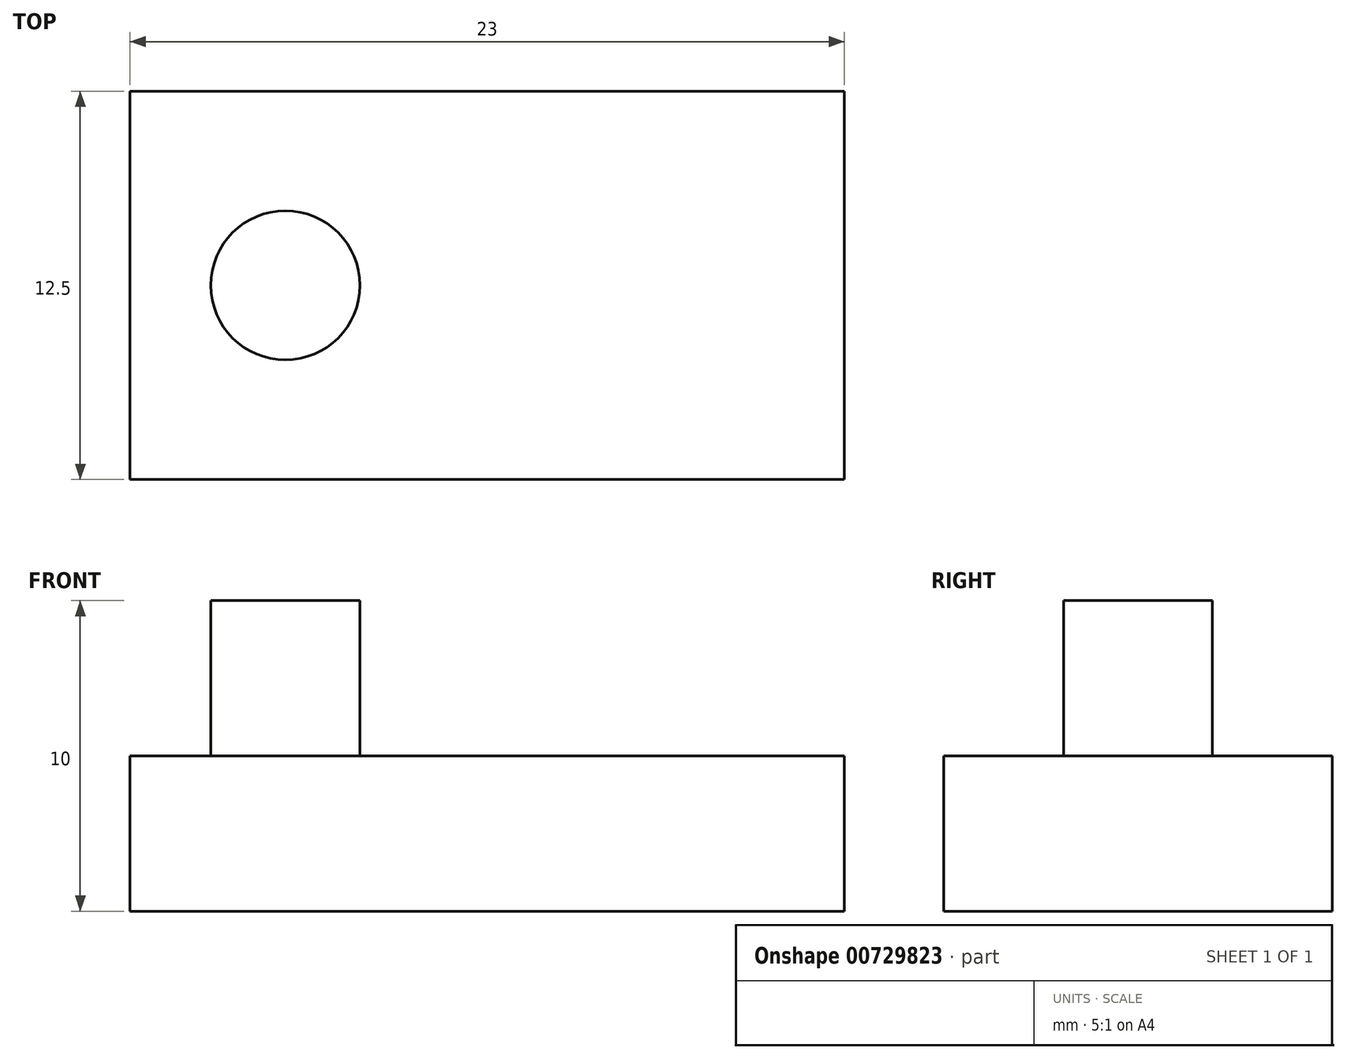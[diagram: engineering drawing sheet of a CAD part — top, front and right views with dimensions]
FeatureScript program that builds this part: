
annotation { "Feature Type Name" : "Feature", "Feature Type Description" : "" }
export const myFeature = defineFeature(function(context is Context, id is Id, definition is map)
    precondition{}
    {
        {
            var Q0;
            Q0=qCreatedBy(makeId("Top.planeOp"),FACE);
            var sketch = newSketch(context, id + "F0", { "sketchPlane" : qUnion([Q0])});
            skLineSegment(sketch, "E0.bottom", {"start": v(11.5, 6.25) * mm, "end": v(-11.5, 6.25) * mm});
            skLineSegment(sketch, "E0.top", {"start": v(11.5, -6.25) * mm, "end": v(-11.5, -6.25) * mm});
            skLineSegment(sketch, "E0.left", {"start": v(11.5, 6.25) * mm, "end": v(11.5, -6.25) * mm});
            skLineSegment(sketch, "E0.right", {"start": v(-11.5, 6.25) * mm, "end": v(-11.5, -6.25) * mm});
            skPoint(sketch, "E0.middle", {"position": v(0, 0) * mm});
            skCircle(sketch, "E1", {"center": v(-6.5, 0) * mm, "radius": 2.4 * mm});
            skPoint(sketch, "E1.centerSnap0", {"position": v(-11.5, 0) * mm});
            skSolve(sketch);
        }
        {
            var Q0;
            Q0=makeQuery(id+"F0.imprint","IMPRINT",FACE,{"disambiguationData":[TD([[makeQuery(id+"F0.imprint","IMPRINT",EDGE,{"derivedFrom":sQuery(id+"F0.wireOp",EDGE,"E0.bottom")}),1.0]])]});
            extrude(context, id + "F1", {"entities" : qUnion([Q0]), "depth" : 5 * mm, "offsetDistance" : 25 * mm});
        }
        {
            var Q0;
            Q0=makeQuery(id+"F0.imprint","IMPRINT",FACE,{"disambiguationData":[TD([[makeQuery(id+"F0.imprint","IMPRINT",EDGE,{"derivedFrom":sQuery(id+"F0.wireOp",EDGE,"E1")}),1.0]])]});
            extrude(context, id + "F2", {"entities" : qUnion([Q0]), "operationType" : NewBodyOperationType.ADD, "depth" : 10 * mm, "offsetDistance" : 25 * mm});
        }
    });
